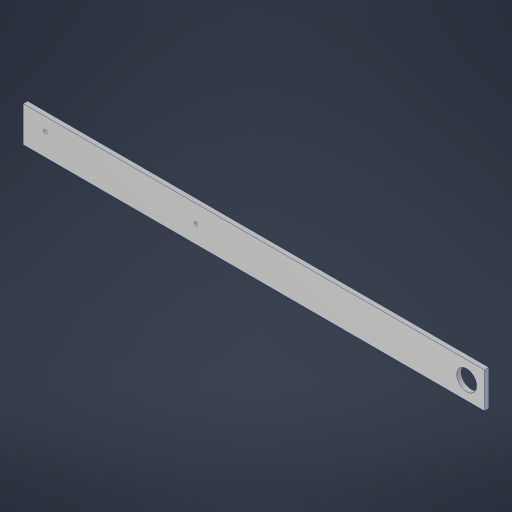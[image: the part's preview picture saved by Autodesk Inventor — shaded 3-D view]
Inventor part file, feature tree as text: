
AUTODESK INVENTOR PART (.ipt)
format: ipt  version: 2023.4 (Build 274418000, 418)  size: 185,856 bytes
history: native  units: in
note: dims shown in document units (in); Inventor stores cm internally (conversion verified against a paired STEP export)
features: sketch x1, extrude x1, hole x1
ambient origin geometry x8: Origin, YZ Plane, XZ Plane, XY Plane, X Axis, Y Axis, Z Axis, Center Point
bodies: Solid1 (feature_tree)
feature tree (3):
  sketch  "Sketch1"  dims[d0=26.0in d1=2.0in d3=1.125in d4=7.375in d5=24.0in d6=8.5in d7=0.25in d10=1.125in d11=1.0in d12=0.25in d13=0.0in d14=0.201in d15=0.75in d16=0.385in d17=0.25in d18=0.5635in d19=1.0in d20=0.8108in d26=1.25in d27=0.75in d28=1.125in]
  extrude  "Extrusion1"  Depth=2.0in
  hole  "Hole1"  [1 undecoded]
note: 1 required parameter value undecoded (feature->parameter linkage not recoverable at this tier; creation-order binding heuristic only, values carry confidence <= 0.55)
